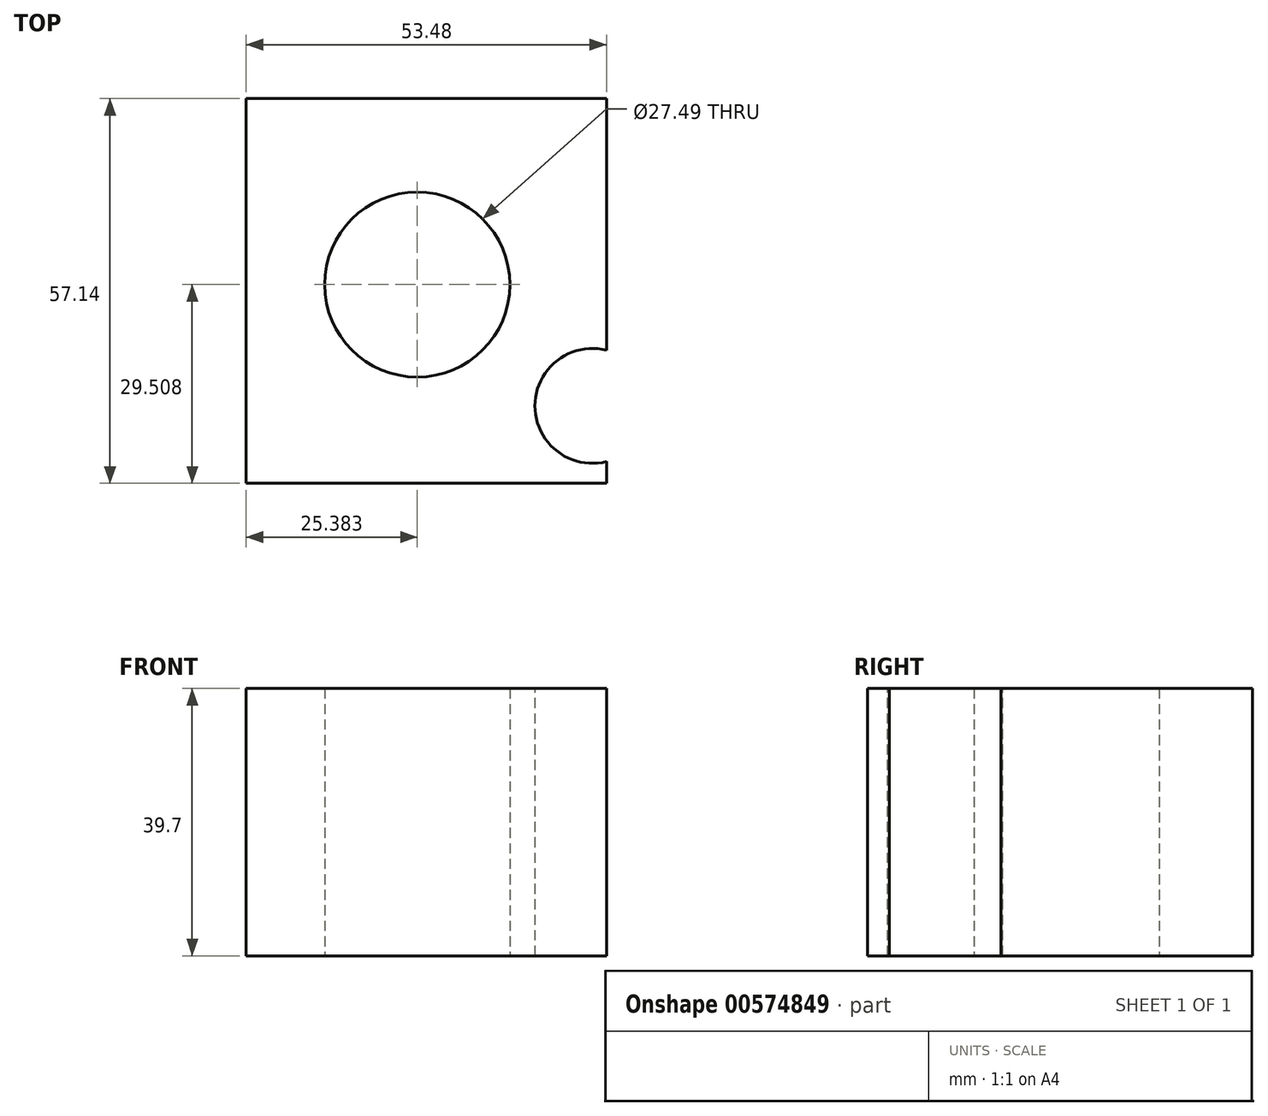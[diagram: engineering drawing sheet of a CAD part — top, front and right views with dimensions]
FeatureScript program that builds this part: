
annotation { "Feature Type Name" : "Feature", "Feature Type Description" : "" }
export const myFeature = defineFeature(function(context is Context, id is Id, definition is map)
    precondition{}
    {
        {
            var Q0;
            Q0=qCreatedBy(makeId("Top.planeOp"),FACE);
            var sketch = newSketch(context, id + "F0", { "sketchPlane" : qUnion([Q0])});
            skLineSegment(sketch, "E0.bottom", {"start": v(-54.4, 45.65) * mm, "end": v(-0.9, 45.65) * mm});
            skLineSegment(sketch, "E0.top", {"start": v(-54.4, -11.49) * mm, "end": v(-0.9, -11.49) * mm});
            skLineSegment(sketch, "E0.left", {"start": v(-54.4, 45.65) * mm, "end": v(-54.4, -11.49) * mm});
            skLineSegment(sketch, "E0.right", {"start": v(-0.9, 45.65) * mm, "end": v(-0.9, -11.49) * mm});
            skCircle(sketch, "E1", {"center": v(-29, 18.02) * mm, "radius": 13.75 * mm});
            skSolve(sketch);
        }
        {
            var Q0;
            Q0=makeQuery(id+"F0.imprint","IMPRINT",FACE,{"disambiguationData":[TD([[makeQuery(id+"F0.imprint","IMPRINT",EDGE,{"derivedFrom":sQuery(id+"F0.wireOp",EDGE,"E0.bottom")}),-1.0]])]});
            extrude(context, id + "F1", {"entities" : qUnion([Q0]), "depth" : 25.4 * mm, "offsetDistance" : 25.4 * mm});
        }
        {
            var Q0;
            Q0=makeQuery(id+"F1.opExtrude","CAP_FACE",FACE,{"disambiguationData":[OSD([sQuery(id+"F0.wireOp",EDGE,"E0.bottom"),sQuery(id+"F0.wireOp",EDGE,"E0.top"),sQuery(id+"F0.wireOp",EDGE,"E0.left"),sQuery(id+"F0.wireOp",EDGE,"E0.right"),sQuery(id+"F0.wireOp",EDGE,"E1")])],"isStart":false});
            var sketch = newSketch(context, id + "F2", { "sketchPlane" : qUnion([Q0])});
            skCircle(sketch, "E2", {"center": v(-3, 0) * mm, "radius": 8.53 * mm});
            skSolve(sketch);
        }
        {
            var Q0;
            Q0 = qSketchRegion(id + "F2", true);
            extrude(context, id + "F3", {"entities" : qUnion([Q0]), "operationType" : NewBodyOperationType.REMOVE, "endBound" : BoundingType.THROUGH_ALL, "oppositeDirection" : true, "depth" : 25.4 * mm, "offsetDistance" : 25.4 * mm});
        }
        {
            var Q0;
            Q0=makeQuery(id+"F1.opExtrude","CAP_FACE",FACE,{"disambiguationData":[OSD([sQuery(id+"F0.wireOp",EDGE,"E0.bottom"),sQuery(id+"F0.wireOp",EDGE,"E0.top"),sQuery(id+"F0.wireOp",EDGE,"E0.left"),sQuery(id+"F0.wireOp",EDGE,"E0.right"),sQuery(id+"F0.wireOp",EDGE,"E1")])],"isStart":false});
            extrude(context, id + "F4", {"entities" : qUnion([Q0]), "operationType" : NewBodyOperationType.ADD, "depth" : 14.3 * mm, "offsetDistance" : 25 * mm});
        }
    });
